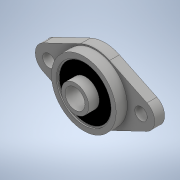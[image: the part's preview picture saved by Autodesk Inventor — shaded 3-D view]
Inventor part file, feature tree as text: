
AUTODESK INVENTOR PART (.ipt)
format: ipt  version: 2020 (Build 240168000, 168)  size: 172,032 bytes
history: native  units: mm
features: extrude x5, sketch x5
ambient origin geometry x8: Origin, YZ Plane, XZ Plane, XY Plane, X Axis, Y Axis, Z Axis, Center Point
bodies: Solid1 (feature_tree)
feature tree (10):
  extrude  "Extrusion1"  Depth=27.0mm
  extrude  "Extrusion2"  Depth=5.0mm
  extrude  "Extrusion3"  Depth=18.5mm
  extrude  "Extrusion4"  Depth=4.0mm TaperAngle=0.0deg
  extrude  "Extrusion5"  Depth=4.5mm TaperAngle=0.0deg
  sketch  "Sketch1"  dims[d0=8.0mm d1=27.0mm]
  sketch  "Sketch2"  dims[d2=5.0mm d3=5.0mm]
  sketch  "Sketch3"  dims[d4=37.0mm d5=18.5mm]
  sketch  "Sketch4"  dims[d8=11.0mm d9=4.0mm d10=0.0mm]
  sketch  "Sketch5"  dims[d11=26.0mm d12=4.5mm d13=0.0mm d14=11.0mm d15=3.5mm d16=0.0mm d17=22.0mm d18=0.5mm d19=0.0mm d20=21.0mm d21=0.2mm d22=0.0mm]
